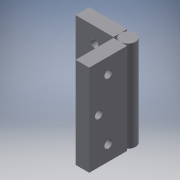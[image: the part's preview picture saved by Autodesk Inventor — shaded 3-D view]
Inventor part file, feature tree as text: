
AUTODESK INVENTOR PART (.ipt)
format: ipt  version: 2016 (Build 200138000, 138)  size: 142,848 bytes
history: native  units: in
note: dims shown in document units (in); Inventor stores cm internally (conversion verified against a paired STEP export)
features: sketch x4, extrude x2, hole x2
ambient origin geometry x8: Origin, YZ Plane, XZ Plane, XY Plane, X Axis, Y Axis, Z Axis, Center Point
bodies: Solid1 (feature_tree)
feature tree (8):
  extrude  "Extrusion1"  Depth=1.25in
  extrude  "Extrusion2"  Depth=0.45in
  sketch  "Sketch3"  dims[d5=1.25in d6=0.45in]
  sketch  "Sketch4"  dims[d7=3.0in d8=0.0in d9=0.25in d10=0.3125in d11=0.25in d12=0.25in d13=1.0in d14=1.0in d15=0.25in d16=0.3125in d17=1.0in d18=1.0in d19=0.25in d20=0.25in d21=0.25in d22=0.75in d23=0.375in d24=0.25in d25=0.5635in d26=1.0in d27=0.8108in d28=0.25in d29=0.75in d30=0.375in d31=0.25in d32=0.5635in d33=1.0in d34=0.8108in]
  hole  "Hole1"  [1 undecoded]
  hole  "Hole2"  [1 undecoded]
  sketch  "Sketch1"  dims[d0=3.0in d1=1.25in]
  sketch  "Sketch2"  dims[d2=0.45in d3=0.0in d4=0.5in]
note: 2 required parameter values undecoded (feature->parameter linkage not recoverable at this tier; creation-order binding heuristic only, values carry confidence <= 0.55)
